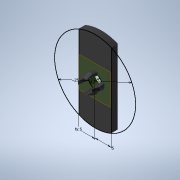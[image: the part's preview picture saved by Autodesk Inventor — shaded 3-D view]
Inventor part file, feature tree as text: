
AUTODESK INVENTOR PART (.ipt)
format: ipt  version: 2022 (Build 260153000, 153)  size: 239,616 bytes
history: native  units: mm
features: thicken_offset x4, extrude x3, plane x2, sketch x2, other x1
ambient origin geometry x8: Origin, YZ Plane, XZ Plane, XY Plane, X Axis, Y Axis, Z Axis, Center Point
bodies: Solid1 (feature_tree)
feature tree (12):
  plane  "Work Plane2"
  extrude  "Extrusion1"  Depth=10.0mm
  sketch  "Sketch2"  dims[d2=0.0mm d3=0.0mm d4=4.2mm d5=25.0mm d6=5.0mm d7=5.0mm d8=2.0mm d9=0.0mm d10=0.0mm d11=0.0mm d12=0.2mm d13=0.2mm d14=0.2mm d15=0.2mm d16=0.2mm d17=0.2mm d18=0.2mm d19=0.2mm]
  extrude  "Extrusion2"  Depth=4.2mm
  extrude  "Extrusion3"  Depth=25.0mm
  thicken_offset  "Thicken1"
  thicken_offset  "Thicken2"
  thicken_offset  "Thicken3"
  thicken_offset  "Thicken4"
  plane  "Work Plane1"
  sketch  "Sketch1"  dims[d0=1.0mm d1=10.0mm]
  other  "Cut-Revolve4"
